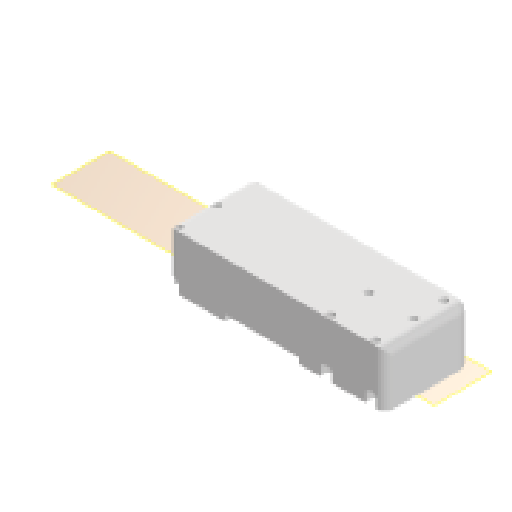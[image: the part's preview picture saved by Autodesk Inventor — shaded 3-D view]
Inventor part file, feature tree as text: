
AUTODESK INVENTOR PART (.ipt)
format: ipt  version: 2024.1 (Build 281209000, 209)  size: 243,712 bytes
history: native  units: mm
features: sketch x4, reference x4, other x4, extrude x3, projected_geometry x2, plane x1, fillet x1, hole x1
ambient origin geometry x8: Origin, YZ Plane, XZ Plane, XY Plane, X Axis, Y Axis, Z Axis, Center Point
bodies: Volumenkörper1 (feature_tree)
feature tree (20):
  plane  "Arbeitsebene1"
  extrude  "Extrusion1"  TaperAngle=0.0deg  [1 undecoded]
  fillet  "Rundung1"  Radius=32.0mm
  hole  "Bohrung1"  [1 undecoded]
  extrude  "Extrusion2"  Depth=18.0mm TaperAngle=0.0deg
  extrude  "Extrusion3"  Depth=27.0mm
  sketch  "Skizze1"  dims[d0=80.0mm d1=0.0mm d2=32.0mm]
  reference  "Referenz1"
  reference  "Referenz2"
  reference  "Referenz3"
  sketch  "Skizze2"  dims[d3=20.0mm d4=0.0mm d5=3.0mm]
  projected_geometry  "Projizierte Kontur1"
  sketch  "Skizze3"  dims[d6=4.9mm d7=6.0mm d8=4.0mm d9=2.0mm d10=90.0deg d11=4.0mm d12=20.594885mm d13=18.0mm d14=0.0mm]
  projected_geometry  "Projizierte Kontur2"
  sketch  "Skizze4"  dims[d15=27.0mm d16=18.0mm d17=18.0mm d18=0.0mm]
  reference  "Referenz4"
  other  "Assembly_HoliSheet_v6.iam"
  other  "10_Wellplate_base_v6:1"
  other  "Assemlby_lightsheet_generator_passive_v2:1"
  other  "30_Lightsheet_generator_singlegalvo:1"
note: 2 required parameter values undecoded (feature->parameter linkage not recoverable at this tier; creation-order binding heuristic only, values carry confidence <= 0.55)
